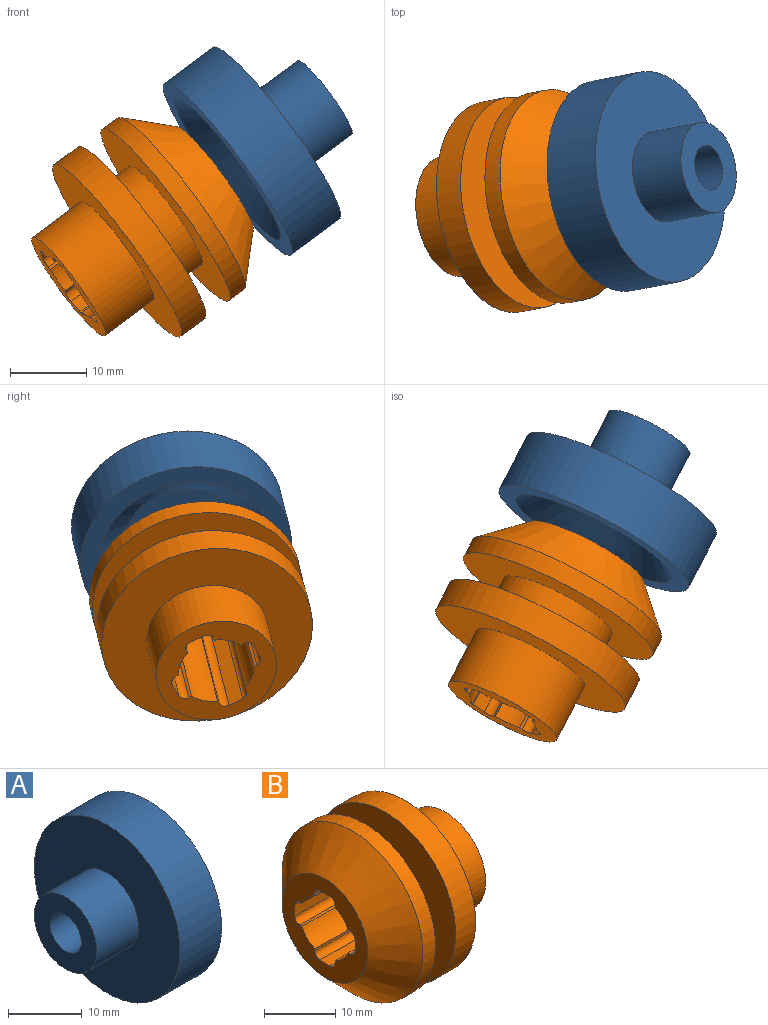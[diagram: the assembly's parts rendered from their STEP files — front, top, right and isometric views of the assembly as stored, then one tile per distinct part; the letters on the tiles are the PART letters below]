
ASSEMBLY  parts=2 mates=1
PART A: 8 faces, bbox 16x28x28 mm
  f0: plane 15x15mm, normal (1,0,0), area 148.4mm2, adj f1,f5
  f1: cone r=7.5mm half-angle=45deg, axis (1,0,0), area 337.7mm2, adj f0,f2
  f2: plane 28x28mm, normal (1,0,0), area 200.3mm2, adj f1,f3
  f3: cylinder r=14mm len=28mm, axis (-1,0,0), area 703.7mm2, adj f2,f4
  f4: plane 28x28mm, normal (-1,0,0), area 502.7mm2, adj f3,f6
  f5: cylinder r=3mm len=12mm, axis (-1,0,0), area 226.2mm2, adj f0,f7
  f6: cylinder r=6mm len=12mm, axis (1,0,0), area 301.6mm2, adj f4,f7
  f7: plane 12x12mm, normal (-1,0,0), area 84.8mm2, adj f5,f6
PART B: 34 faces, bbox 24x28x28 mm
  f0: cylinder r=5mm len=24mm, axis (1,0,0), area 89.7mm2, adj f4,f18,f27,f28
  f1: cylinder r=1mm len=24mm, axis (-1,0,0), area 37.7mm2, adj f3,f5,f18,f27
  f2: cylinder r=1mm len=24mm, axis (1,0,0), area 37.7mm2, adj f3,f4,f18,f27
  f3: plane 24x2mm, normal (0,0,1), area 48mm2, adj f1,f2,f18,f27
  f4: plane 24x0.42mm, normal (0,-1,0), area 10mm2, adj f0,f2,f18,f27
  f5: plane 24x0.42mm, normal (0,1,0), area 10mm2, adj f1,f6,f18,f27
  f6: cylinder r=5mm len=24mm, axis (1,0,0), area 89.7mm2, adj f5,f10,f18,f27
  f7: cylinder r=1mm len=24mm, axis (-1,0,0), area 37.7mm2, adj f9,f11,f18,f27
  f8: cylinder r=1mm len=24mm, axis (1,0,0), area 37.7mm2, adj f9,f10,f18,f27
  f9: plane 24x2mm, normal (0,1,0), area 48mm2, adj f7,f8,f18,f27
  f10: plane 24x0.42mm, normal (0,0,1), area 10mm2, adj f6,f8,f18,f27
  f11: plane 24x0.42mm, normal (0,0,-1), area 10mm2, adj f7,f12,f18,f27
  f12: cylinder r=5mm len=24mm, axis (1,0,0), area 89.7mm2, adj f11,f16,f18,f27
  f13: cylinder r=1mm len=24mm, axis (-1,0,0), area 37.7mm2, adj f15,f17,f18,f27
  f14: cylinder r=1mm len=24mm, axis (1,0,0), area 37.7mm2, adj f15,f16,f18,f27
  f15: plane 24x2mm, normal (0,0,-1), area 48mm2, adj f13,f14,f18,f27
  f16: plane 24x0.42mm, normal (0,1,0), area 10mm2, adj f12,f14,f18,f27
  f17: plane 24x0.42mm, normal (0,-1,0), area 10mm2, adj f13,f18,f27,f33
  f18: plane 17x17mm, normal (-1,0,0), area 132mm2, adj f0,f1,f2,f3,f4,f5,f6,f7
  f19: plane 28x28mm, normal (1,0,0), area 414.7mm2, adj f20,f22
  f20: cylinder r=14mm len=28mm, axis (-1,0,0), area 219.9mm2, adj f19,f21
  f21: cone r=8.5mm half-angle=45deg, axis (1,0,0), area 549.8mm2, adj f18,f20
  f22: cylinder r=8mm len=16mm, axis (-1,0,0), area 201.1mm2, adj f19,f25
  f23: cylinder r=14mm len=28mm, axis (-1,0,0), area 351.9mm2, adj f24,f25
  f24: plane 28x28mm, normal (1,0,0), area 414.7mm2, adj f23,f26
  f25: plane 28x28mm, normal (-1,0,0), area 414.7mm2, adj f22,f23
  f26: cylinder r=8mm len=16mm, axis (-1,0,0), area 402.1mm2, adj f24,f27
  f27: plane 16x16mm, normal (1,0,0), area 106.1mm2, adj f0,f1,f2,f3,f4,f5,f6,f7
  f28: plane 24x0.42mm, normal (0,0,1), area 10mm2, adj f0,f18,f27,f32
  f29: plane 24x2mm, normal (0,-1,0), area 48mm2, adj f18,f27,f31,f32
  f30: plane 24x0.42mm, normal (0,0,-1), area 10mm2, adj f18,f27,f31,f33
  f31: cylinder r=1mm len=24mm, axis (1,0,0), area 37.7mm2, adj f18,f27,f29,f30
  f32: cylinder r=1mm len=24mm, axis (-1,0,0), area 37.7mm2, adj f18,f27,f28,f29
  f33: cylinder r=5mm len=24mm, axis (1,0,0), area 89.7mm2, adj f17,f18,f27,f30
PLACE A rot(axis=(0,0.97,-0.25),142.7deg) t=(-24.69,-2.25,-12.13)mm fixed
PLACE B rot(axis=(-0.23,0.84,0.5),153.8deg) t=(-17.77,-2.02,-9.25)mm
MATE fastened B.f20 <-> A.f1  axis (-0.8,-0.15,-0.59) through (-27.09,-3.79,-16.14)mm
